# Revit family: Hager-Panelboard_400A_Incoming_125A_Outgoing-UK-en
name_source: partatom
category: Electrical Equipment
units: mm (PartAtom-declared; Revit-internal decimal feet)

## family parameters
Cut with Voids When Loaded = No
Host = Face
Panel Configuration = Two Columns, Circuits Across
Part Type = Panelboard
Room Calculation Point = No
Round Connector Dimension = Use Diameter
Shared = No

## types (10) — shared parameters
Classification.Uniclass.Pr.Description = Control circuit device enclosures
Classification.Uniclass.Pr.Number = Pr_80_77_28_16
EF000003 - Mounting method = EV000384 - Surface mounted (plaster)
EF000008 - Width = 900 mm  [stored 2.95276 ft]
EF000049 - Depth = 220 mm  [stored 0.721785 ft]
EF000118 - With mounting plate = No
EF001062 - EMC-version = No
EF001088 - Extension possible = No
EF001134 - DIN-rail = No
EF006306 - With lock = Yes
EF015776 - Earthing terminal block = Yes
EF015777 - Neutral terminal block = Yes
EF015941 - Signal passing door = No
HG000002 - With door or cover = Yes
HG000003 - Range = Panelboards
HG000005 - Thickness = 3 mm  [stored 0.00984252 ft]
HG000017 - Distance between poles = 25 mm  [stored 0.082021 ft]
Manufacturer = Hager
Type Comments = Panelboards
zero-valued in all types: Default Elevation, EF000218 - Built-in depth, EF000266 - Number of rows, EF000332 - Built-in height, EF000846 - Built-in width, EF001131 - Internal depth

## per-type parameters (varying)
| type | EF000007 - Colour | EF000040 - Height | EF000339 - Type of cover | EF001596 - Material housing | EF002950 - Width in number of modular spacings | EF004462 - Type of closure | EF005474 - Degree of protection (IP) | EF006244 - Transparent cover/door | HG000004 - Manufacturer reference | Model |
| Surface mounted  W900 H1250 D220 9 Modular spacings - JF406B |  | 1250 mm  [stored 4.10105 ft] | EV001012 - Cover |  | 9 |  |  | No | JF406B | JF406B |
| Surface mounted IP30 W900 H1250 D220 12 Modular spacings - JF408B | EV000154 - Other | 1250 mm  [stored 4.10105 ft] | EV004216 - Door | EV000179 - Steel | 12 | EV001412 - Cylinder | EV006410 - IP30 | No | JF408B | JF408B |
| Surface mounted IP30 W900 H1250 D220 12 Modular spacings - JF408BG | EV000154 - Other | 1250 mm  [stored 4.10105 ft] | EV004216 - Door | EV000179 - Steel | 12 | EV001412 - Cylinder | EV006410 - IP30 | Yes | JF408BG | JF408BG |
| Surface mounted IP30 W900 H1250 D220 9 Modular spacings - JF406BG | EV000154 - Other | 1250 mm  [stored 4.10105 ft] | EV004216 - Door | EV000179 - Steel | 9 | EV001412 - Cylinder | EV006410 - IP30 | Yes | JF406BG | JF406BG |
| Surface mounted IP30 W900 H1400 D220 18 Modular spacings - JF412B | EV000154 - Other | 1400 mm | EV004216 - Door | EV000179 - Steel | 18 | EV001412 - Cylinder | EV006410 - IP30 | No | JF412B | JF412B |
| Surface mounted IP30 W900 H1400 D220 18 Modular spacings - JF412BG | EV000154 - Other | 1400 mm | EV004216 - Door | EV000179 - Steel | 18 | EV001412 - Cylinder | EV006410 - IP30 | Yes | JF412BG | JF412BG |
| Surface mounted IP30 W900 H1550 D220 24 Modular spacings - JF416B | EV000154 - Other | 1550 mm | EV004216 - Door | EV000179 - Steel | 24 | EV001412 - Cylinder | EV006410 - IP30 | No | JF416B | JF416B |
| Surface mounted IP30 W900 H1550 D220 24 Modular spacings - JF416BG | EV000154 - Other | 1550 mm | EV004216 - Door | EV000179 - Steel | 24 | EV001412 - Cylinder | EV006410 - IP30 | Yes | JF416BG | JF416BG |
| Surface mounted IP30 W900 H1700 D220 27 Modular spacings - JF418B | EV000154 - Other | 1700 mm  [stored 5.57743 ft] | EV004216 - Door | EV000179 - Steel | 27 | EV001412 - Cylinder | EV006410 - IP30 | No | JF418B | JF418B |
| Surface mounted IP30 W900 H1700 D220 27 Modular spacings - JF418BG | EV000154 - Other | 1700 mm  [stored 5.57743 ft] | EV004216 - Door | EV000179 - Steel | 27 | EV001412 - Cylinder | EV006410 - IP30 | Yes | JF418BG | JF418BG |

note: [stored X ft] marks values corroborated as IEEE doubles in the binary element streams (Revit-internal decimal feet)

## geometry (parser evidence)
native form markers: Sweep x8
no freeform markers — native parametric forms only
